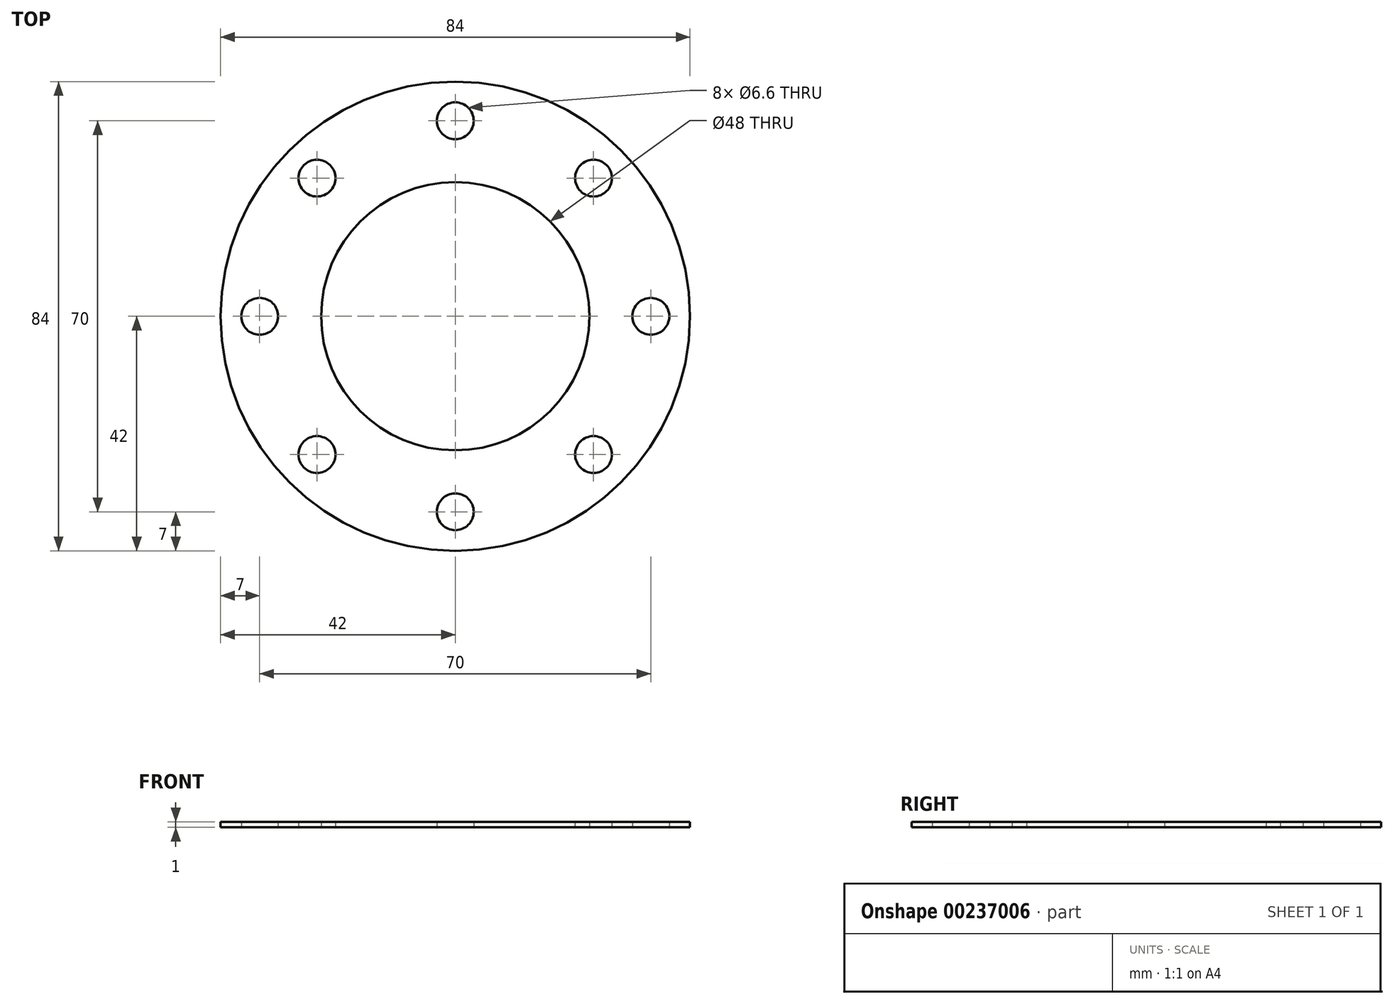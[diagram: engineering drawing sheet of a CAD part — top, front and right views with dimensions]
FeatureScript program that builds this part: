
annotation { "Feature Type Name" : "Feature", "Feature Type Description" : "" }
export const myFeature = defineFeature(function(context is Context, id is Id, definition is map)
    precondition{}
    {
        {
            var Q0;
            Q0=qCreatedBy(makeId("Top.planeOp"),FACE);
            var sketch = newSketch(context, id + "F0", { "sketchPlane" : qUnion([Q0])});
            skCircle(sketch, "E0", {"center": v(0, 0) * mm, "radius": 24 * mm});
            skCircle(sketch, "E1", {"center": v(0, 0) * mm, "radius": 42 * mm});
            skSolve(sketch);
        }
        {
            var Q0;
            Q0=makeQuery(id+"F0.imprint","IMPRINT",FACE,{"disambiguationData":[TD([[makeQuery(id+"F0.imprint","IMPRINT",EDGE,{"derivedFrom":sQuery(id+"F0.wireOp",EDGE,"E0")}),-1.0]])]});
            extrude(context, id + "F1", {"entities" : qUnion([Q0]), "depth" : 1 * mm});
        }
        {
            var Q0;
            Q0=qCreatedBy(makeId("Top.planeOp"),FACE);
            var sketch = newSketch(context, id + "F2", { "sketchPlane" : qUnion([Q0])});
            skCircle(sketch, "E2", {"center": v(0, 0) * mm, "radius": 35 * mm});
            skCircle(sketch, "E3", {"center": v(-35, 0) * mm, "radius": 3.3 * mm});
            skCircle(sketch, "E4", {"center": v(0, 35) * mm, "radius": 3.3 * mm});
            skLineSegment(sketch, "E5", {"start": v(-35, 0) * mm, "end": v(0, 35) * mm});
            skLineSegment(sketch, "E6", {"start": v(-17.5, 17.5) * mm, "end": v(0, 0) * mm});
            skLineSegment(sketch, "E7", {"start": v(-17.5, 17.5) * mm, "end": v(-29.4, 29.4) * mm});
            skCircle(sketch, "E8", {"center": v(-24.75, 24.75) * mm, "radius": 3.3 * mm});
            skLineSegment(sketch, "E9", {"start": v(0, 0) * mm, "end": v(29.13, -29.13) * mm});
            skCircle(sketch, "E10", {"center": v(35, 0) * mm, "radius": 3.3 * mm});
            skCircle(sketch, "E11", {"center": v(24.75, -24.75) * mm, "radius": 3.3 * mm});
            skCircle(sketch, "E12", {"center": v(0, -35) * mm, "radius": 3.3 * mm});
            skLineSegment(sketch, "E13", {"start": v(-35, 0) * mm, "end": v(0, -35) * mm});
            skLineSegment(sketch, "E14", {"start": v(0, 0) * mm, "end": v(-17.5, -17.5) * mm});
            skLineSegment(sketch, "E15", {"start": v(-17.5, -17.5) * mm, "end": v(-30.67, -30.67) * mm});
            skLineSegment(sketch, "E16", {"start": v(0, 0) * mm, "end": v(29.69, 29.69) * mm});
            skCircle(sketch, "E17", {"center": v(-24.75, -24.75) * mm, "radius": 3.3 * mm});
            skCircle(sketch, "E18", {"center": v(24.75, 24.75) * mm, "radius": 3.3 * mm});
            skSolve(sketch);
        }
        {
            var Q0;
            {var subQ0=sQuery(id+"F2.wireOp",EDGE,"E10");var subQ1=sQuery(id+"F2.wireOp",EDGE,"E2");var subQ2=makeQuery(id+"F2.imprint","INTERSECT",VERTEX,{"disambiguationData":[OD(0.0)],"derivedFrom":[subQ1,subQ0]});Q0=makeQuery(id+"F2.imprint","IMPRINT",FACE,{"disambiguationData":[TD([[makeQuery(id+"F2.imprint","IMPRINT",EDGE,{"disambiguationData":[TD([[subQ2,1.0]])],"derivedFrom":subQ1}),-1.0]])]});}
            var Q1;
            {var subQ0=sQuery(id+"F2.wireOp",EDGE,"E18");var subQ1=sQuery(id+"F2.wireOp",EDGE,"E2");var subQ2=makeQuery(id+"F2.imprint","INTERSECT",VERTEX,{"disambiguationData":[OD(0.0)],"derivedFrom":[subQ1,subQ0]});Q1=makeQuery(id+"F2.imprint","IMPRINT",FACE,{"disambiguationData":[TD([[makeQuery(id+"F2.imprint","IMPRINT",EDGE,{"disambiguationData":[TD([[subQ2,-1.0]])],"derivedFrom":subQ1}),-1.0]])]});}
            var Q2;
            {var subQ0=sQuery(id+"F2.wireOp",EDGE,"E18");var subQ1=sQuery(id+"F2.wireOp",EDGE,"E2");var subQ2=makeQuery(id+"F2.imprint","INTERSECT",VERTEX,{"disambiguationData":[OD(1.0)],"derivedFrom":[subQ1,subQ0]});Q2=makeQuery(id+"F2.imprint","IMPRINT",FACE,{"disambiguationData":[TD([[makeQuery(id+"F2.imprint","IMPRINT",EDGE,{"disambiguationData":[TD([[subQ2,1.0]])],"derivedFrom":subQ1}),-1.0]])]});}
            var Q3;
            {var subQ0=sQuery(id+"F2.wireOp",EDGE,"E2");var subQ1=makeQuery(id+"F2.imprint","INTERSECT",VERTEX,{"derivedFrom":[subQ0,sQuery(id+"F2.wireOp",EDGE,"E5")]});Q3=makeQuery(id+"F2.imprint","IMPRINT",FACE,{"disambiguationData":[TD([[makeQuery(id+"F2.imprint","IMPRINT",EDGE,{"disambiguationData":[TD([[subQ1,1.0]])],"derivedFrom":subQ0}),-1.0]])]});}
            var Q4;
            {var subQ0=sQuery(id+"F2.wireOp",EDGE,"E8");var subQ1=sQuery(id+"F2.wireOp",EDGE,"E2");var subQ2=makeQuery(id+"F2.imprint","INTERSECT",VERTEX,{"disambiguationData":[OD(0.0)],"derivedFrom":[subQ1,subQ0]});Q4=makeQuery(id+"F2.imprint","IMPRINT",FACE,{"disambiguationData":[TD([[makeQuery(id+"F2.imprint","IMPRINT",EDGE,{"disambiguationData":[TD([[subQ2,-1.0]])],"derivedFrom":subQ1}),-1.0]])]});}
            var Q5;
            {var subQ0=sQuery(id+"F2.wireOp",EDGE,"E8");var subQ1=sQuery(id+"F2.wireOp",EDGE,"E2");var subQ2=makeQuery(id+"F2.imprint","INTERSECT",VERTEX,{"disambiguationData":[OD(1.0)],"derivedFrom":[subQ1,subQ0]});Q5=makeQuery(id+"F2.imprint","IMPRINT",FACE,{"disambiguationData":[TD([[makeQuery(id+"F2.imprint","IMPRINT",EDGE,{"disambiguationData":[TD([[subQ2,1.0]])],"derivedFrom":subQ1}),-1.0]])]});}
            var Q6;
            {var subQ0=sQuery(id+"F2.wireOp",EDGE,"E2");var subQ2=sQuery(id+"F2.wireOp",EDGE,"E3");var subQ3=makeQuery(id+"F2.imprint","INTERSECT",VERTEX,{"disambiguationData":[OD(0.0)],"derivedFrom":[subQ0,subQ2]});Q6=makeQuery(id+"F2.imprint","IMPRINT",FACE,{"disambiguationData":[TD([[makeQuery(id+"F2.imprint","IMPRINT",EDGE,{"disambiguationData":[TD([[subQ3,-1.0]])],"derivedFrom":subQ2}),1.0]])]});}
            var Q7;
            {var subQ0=sQuery(id+"F2.wireOp",EDGE,"E17");var subQ1=sQuery(id+"F2.wireOp",EDGE,"E2");var subQ2=makeQuery(id+"F2.imprint","INTERSECT",VERTEX,{"disambiguationData":[OD(0.0)],"derivedFrom":[subQ1,subQ0]});Q7=makeQuery(id+"F2.imprint","IMPRINT",FACE,{"disambiguationData":[TD([[makeQuery(id+"F2.imprint","IMPRINT",EDGE,{"disambiguationData":[TD([[subQ2,-1.0]])],"derivedFrom":subQ1}),-1.0]])]});}
            var Q8;
            {var subQ0=sQuery(id+"F2.wireOp",EDGE,"E17");var subQ1=sQuery(id+"F2.wireOp",EDGE,"E2");var subQ2=makeQuery(id+"F2.imprint","INTERSECT",VERTEX,{"disambiguationData":[OD(1.0)],"derivedFrom":[subQ1,subQ0]});Q8=makeQuery(id+"F2.imprint","IMPRINT",FACE,{"disambiguationData":[TD([[makeQuery(id+"F2.imprint","IMPRINT",EDGE,{"disambiguationData":[TD([[subQ2,1.0]])],"derivedFrom":subQ1}),-1.0]])]});}
            var Q9;
            {var subQ0=sQuery(id+"F2.wireOp",EDGE,"E2");var subQ1=makeQuery(id+"F2.imprint","INTERSECT",VERTEX,{"derivedFrom":[subQ0,sQuery(id+"F2.wireOp",EDGE,"E13")]});Q9=makeQuery(id+"F2.imprint","IMPRINT",FACE,{"disambiguationData":[TD([[makeQuery(id+"F2.imprint","IMPRINT",EDGE,{"disambiguationData":[TD([[subQ1,1.0]])],"derivedFrom":subQ0}),-1.0]])]});}
            var Q10;
            {var subQ0=sQuery(id+"F2.wireOp",EDGE,"E11");var subQ1=sQuery(id+"F2.wireOp",EDGE,"E2");var subQ2=makeQuery(id+"F2.imprint","INTERSECT",VERTEX,{"disambiguationData":[OD(0.0)],"derivedFrom":[subQ1,subQ0]});Q10=makeQuery(id+"F2.imprint","IMPRINT",FACE,{"disambiguationData":[TD([[makeQuery(id+"F2.imprint","IMPRINT",EDGE,{"disambiguationData":[TD([[subQ2,-1.0]])],"derivedFrom":subQ1}),-1.0]])]});}
            var Q11;
            {var subQ0=sQuery(id+"F2.wireOp",EDGE,"E11");var subQ1=sQuery(id+"F2.wireOp",EDGE,"E2");var subQ2=makeQuery(id+"F2.imprint","INTERSECT",VERTEX,{"disambiguationData":[OD(1.0)],"derivedFrom":[subQ1,subQ0]});Q11=makeQuery(id+"F2.imprint","IMPRINT",FACE,{"disambiguationData":[TD([[makeQuery(id+"F2.imprint","IMPRINT",EDGE,{"disambiguationData":[TD([[subQ2,1.0]])],"derivedFrom":subQ1}),-1.0]])]});}
            var Q12;
            {var subQ0=sQuery(id+"F2.wireOp",EDGE,"E10");var subQ1=sQuery(id+"F2.wireOp",EDGE,"E2");var subQ2=makeQuery(id+"F2.imprint","INTERSECT",VERTEX,{"disambiguationData":[OD(0.0)],"derivedFrom":[subQ1,subQ0]});Q12=makeQuery(id+"F2.imprint","IMPRINT",FACE,{"disambiguationData":[TD([[makeQuery(id+"F2.imprint","IMPRINT",EDGE,{"disambiguationData":[TD([[subQ2,1.0]])],"derivedFrom":subQ1}),1.0]])]});}
            var Q13;
            {var subQ0=sQuery(id+"F2.wireOp",EDGE,"E18");var subQ1=sQuery(id+"F2.wireOp",EDGE,"E2");var subQ2=makeQuery(id+"F2.imprint","INTERSECT",VERTEX,{"disambiguationData":[OD(0.0)],"derivedFrom":[subQ1,subQ0]});Q13=makeQuery(id+"F2.imprint","IMPRINT",FACE,{"disambiguationData":[TD([[makeQuery(id+"F2.imprint","IMPRINT",EDGE,{"disambiguationData":[TD([[subQ2,-1.0]])],"derivedFrom":subQ1}),1.0]])]});}
            var Q14;
            {var subQ0=sQuery(id+"F2.wireOp",EDGE,"E18");var subQ1=sQuery(id+"F2.wireOp",EDGE,"E2");var subQ2=makeQuery(id+"F2.imprint","INTERSECT",VERTEX,{"disambiguationData":[OD(1.0)],"derivedFrom":[subQ1,subQ0]});Q14=makeQuery(id+"F2.imprint","IMPRINT",FACE,{"disambiguationData":[TD([[makeQuery(id+"F2.imprint","IMPRINT",EDGE,{"disambiguationData":[TD([[subQ2,1.0]])],"derivedFrom":subQ1}),1.0]])]});}
            var Q15;
            {var subQ0=sQuery(id+"F2.wireOp",EDGE,"E5");var subQ1=sQuery(id+"F2.wireOp",EDGE,"E2");var subQ2=makeQuery(id+"F2.imprint","INTERSECT",VERTEX,{"derivedFrom":[subQ1,subQ0]});Q15=makeQuery(id+"F2.imprint","IMPRINT",FACE,{"disambiguationData":[TD([[makeQuery(id+"F2.imprint","IMPRINT",EDGE,{"disambiguationData":[TD([[subQ2,1.0]])],"derivedFrom":subQ1}),1.0]])]});}
            var Q16;
            {var subQ0=sQuery(id+"F2.wireOp",EDGE,"E5");var subQ1=sQuery(id+"F2.wireOp",EDGE,"E2");var subQ2=makeQuery(id+"F2.imprint","INTERSECT",VERTEX,{"derivedFrom":[subQ1,subQ0]});Q16=makeQuery(id+"F2.imprint","IMPRINT",FACE,{"disambiguationData":[TD([[makeQuery(id+"F2.imprint","IMPRINT",EDGE,{"disambiguationData":[TD([[subQ2,-1.0]])],"derivedFrom":subQ1}),1.0]])]});}
            var Q17;
            {var subQ0=sQuery(id+"F2.wireOp",EDGE,"E8");var subQ1=sQuery(id+"F2.wireOp",EDGE,"E2");var subQ2=makeQuery(id+"F2.imprint","INTERSECT",VERTEX,{"disambiguationData":[OD(0.0)],"derivedFrom":[subQ1,subQ0]});Q17=makeQuery(id+"F2.imprint","IMPRINT",FACE,{"disambiguationData":[TD([[makeQuery(id+"F2.imprint","IMPRINT",EDGE,{"disambiguationData":[TD([[subQ2,-1.0]])],"derivedFrom":subQ1}),1.0]])]});}
            var Q18;
            {var subQ0=sQuery(id+"F2.wireOp",EDGE,"E8");var subQ1=sQuery(id+"F2.wireOp",EDGE,"E2");var subQ2=makeQuery(id+"F2.imprint","INTERSECT",VERTEX,{"disambiguationData":[OD(1.0)],"derivedFrom":[subQ1,subQ0]});Q18=makeQuery(id+"F2.imprint","IMPRINT",FACE,{"disambiguationData":[TD([[makeQuery(id+"F2.imprint","IMPRINT",EDGE,{"disambiguationData":[TD([[subQ2,1.0]])],"derivedFrom":subQ1}),1.0]])]});}
            var Q19;
            {var subQ1=sQuery(id+"F2.wireOp",EDGE,"E2");var subQ3=sQuery(id+"F2.wireOp",EDGE,"E3");var subQ4=makeQuery(id+"F2.imprint","INTERSECT",VERTEX,{"disambiguationData":[OD(0.0)],"derivedFrom":[subQ1,subQ3]});Q19=makeQuery(id+"F2.imprint","IMPRINT",FACE,{"disambiguationData":[TD([[makeQuery(id+"F2.imprint","IMPRINT",EDGE,{"disambiguationData":[TD([[subQ4,1.0]])],"derivedFrom":subQ3}),1.0]])]});}
            var Q20;
            {var subQ1=sQuery(id+"F2.wireOp",EDGE,"E2");var subQ3=sQuery(id+"F2.wireOp",EDGE,"E3");var subQ4=makeQuery(id+"F2.imprint","INTERSECT",VERTEX,{"disambiguationData":[OD(1.0)],"derivedFrom":[subQ1,subQ3]});Q20=makeQuery(id+"F2.imprint","IMPRINT",FACE,{"disambiguationData":[TD([[makeQuery(id+"F2.imprint","IMPRINT",EDGE,{"disambiguationData":[TD([[subQ4,-1.0]])],"derivedFrom":subQ3}),1.0]])]});}
            var Q21;
            {var subQ0=sQuery(id+"F2.wireOp",EDGE,"E17");var subQ1=sQuery(id+"F2.wireOp",EDGE,"E2");var subQ2=makeQuery(id+"F2.imprint","INTERSECT",VERTEX,{"disambiguationData":[OD(0.0)],"derivedFrom":[subQ1,subQ0]});Q21=makeQuery(id+"F2.imprint","IMPRINT",FACE,{"disambiguationData":[TD([[makeQuery(id+"F2.imprint","IMPRINT",EDGE,{"disambiguationData":[TD([[subQ2,-1.0]])],"derivedFrom":subQ1}),1.0]])]});}
            var Q22;
            {var subQ0=sQuery(id+"F2.wireOp",EDGE,"E17");var subQ1=sQuery(id+"F2.wireOp",EDGE,"E2");var subQ2=makeQuery(id+"F2.imprint","INTERSECT",VERTEX,{"disambiguationData":[OD(1.0)],"derivedFrom":[subQ1,subQ0]});Q22=makeQuery(id+"F2.imprint","IMPRINT",FACE,{"disambiguationData":[TD([[makeQuery(id+"F2.imprint","IMPRINT",EDGE,{"disambiguationData":[TD([[subQ2,1.0]])],"derivedFrom":subQ1}),1.0]])]});}
            var Q23;
            {var subQ0=sQuery(id+"F2.wireOp",EDGE,"E13");var subQ1=sQuery(id+"F2.wireOp",EDGE,"E2");var subQ2=makeQuery(id+"F2.imprint","INTERSECT",VERTEX,{"derivedFrom":[subQ1,subQ0]});Q23=makeQuery(id+"F2.imprint","IMPRINT",FACE,{"disambiguationData":[TD([[makeQuery(id+"F2.imprint","IMPRINT",EDGE,{"disambiguationData":[TD([[subQ2,1.0]])],"derivedFrom":subQ1}),1.0]])]});}
            var Q24;
            {var subQ0=sQuery(id+"F2.wireOp",EDGE,"E13");var subQ1=sQuery(id+"F2.wireOp",EDGE,"E2");var subQ2=makeQuery(id+"F2.imprint","INTERSECT",VERTEX,{"derivedFrom":[subQ1,subQ0]});Q24=makeQuery(id+"F2.imprint","IMPRINT",FACE,{"disambiguationData":[TD([[makeQuery(id+"F2.imprint","IMPRINT",EDGE,{"disambiguationData":[TD([[subQ2,-1.0]])],"derivedFrom":subQ1}),1.0]])]});}
            var Q25;
            {var subQ0=sQuery(id+"F2.wireOp",EDGE,"E11");var subQ1=sQuery(id+"F2.wireOp",EDGE,"E2");var subQ2=makeQuery(id+"F2.imprint","INTERSECT",VERTEX,{"disambiguationData":[OD(0.0)],"derivedFrom":[subQ1,subQ0]});Q25=makeQuery(id+"F2.imprint","IMPRINT",FACE,{"disambiguationData":[TD([[makeQuery(id+"F2.imprint","IMPRINT",EDGE,{"disambiguationData":[TD([[subQ2,-1.0]])],"derivedFrom":subQ1}),1.0]])]});}
            var Q26;
            {var subQ0=sQuery(id+"F2.wireOp",EDGE,"E11");var subQ1=sQuery(id+"F2.wireOp",EDGE,"E2");var subQ2=makeQuery(id+"F2.imprint","INTERSECT",VERTEX,{"disambiguationData":[OD(1.0)],"derivedFrom":[subQ1,subQ0]});Q26=makeQuery(id+"F2.imprint","IMPRINT",FACE,{"disambiguationData":[TD([[makeQuery(id+"F2.imprint","IMPRINT",EDGE,{"disambiguationData":[TD([[subQ2,1.0]])],"derivedFrom":subQ1}),1.0]])]});}
            var Q27;
            {var subQ0=sQuery(id+"F2.wireOp",EDGE,"E5");var subQ1=sQuery(id+"F2.wireOp",EDGE,"E3");var subQ2=makeQuery(id+"F2.imprint","INTERSECT",VERTEX,{"derivedFrom":[subQ1,subQ0]});Q27=makeQuery(id+"F2.imprint","IMPRINT",FACE,{"disambiguationData":[TD([[makeQuery(id+"F2.imprint","IMPRINT",EDGE,{"disambiguationData":[TD([[subQ2,1.0]])],"derivedFrom":subQ1}),1.0]])]});}
            extrude(context, id + "F3", {"entities" : qUnion([Q0, Q1, Q2, Q3, Q4, Q5, Q6, Q7, Q8, Q9, Q10, Q11, Q12, Q13, Q14, Q15, Q16, Q17, Q18, Q19, Q20, Q21, Q22, Q23, Q24, Q25, Q26, Q27]), "operationType" : NewBodyOperationType.REMOVE, "depth" : 25 * mm});
        }
    });
